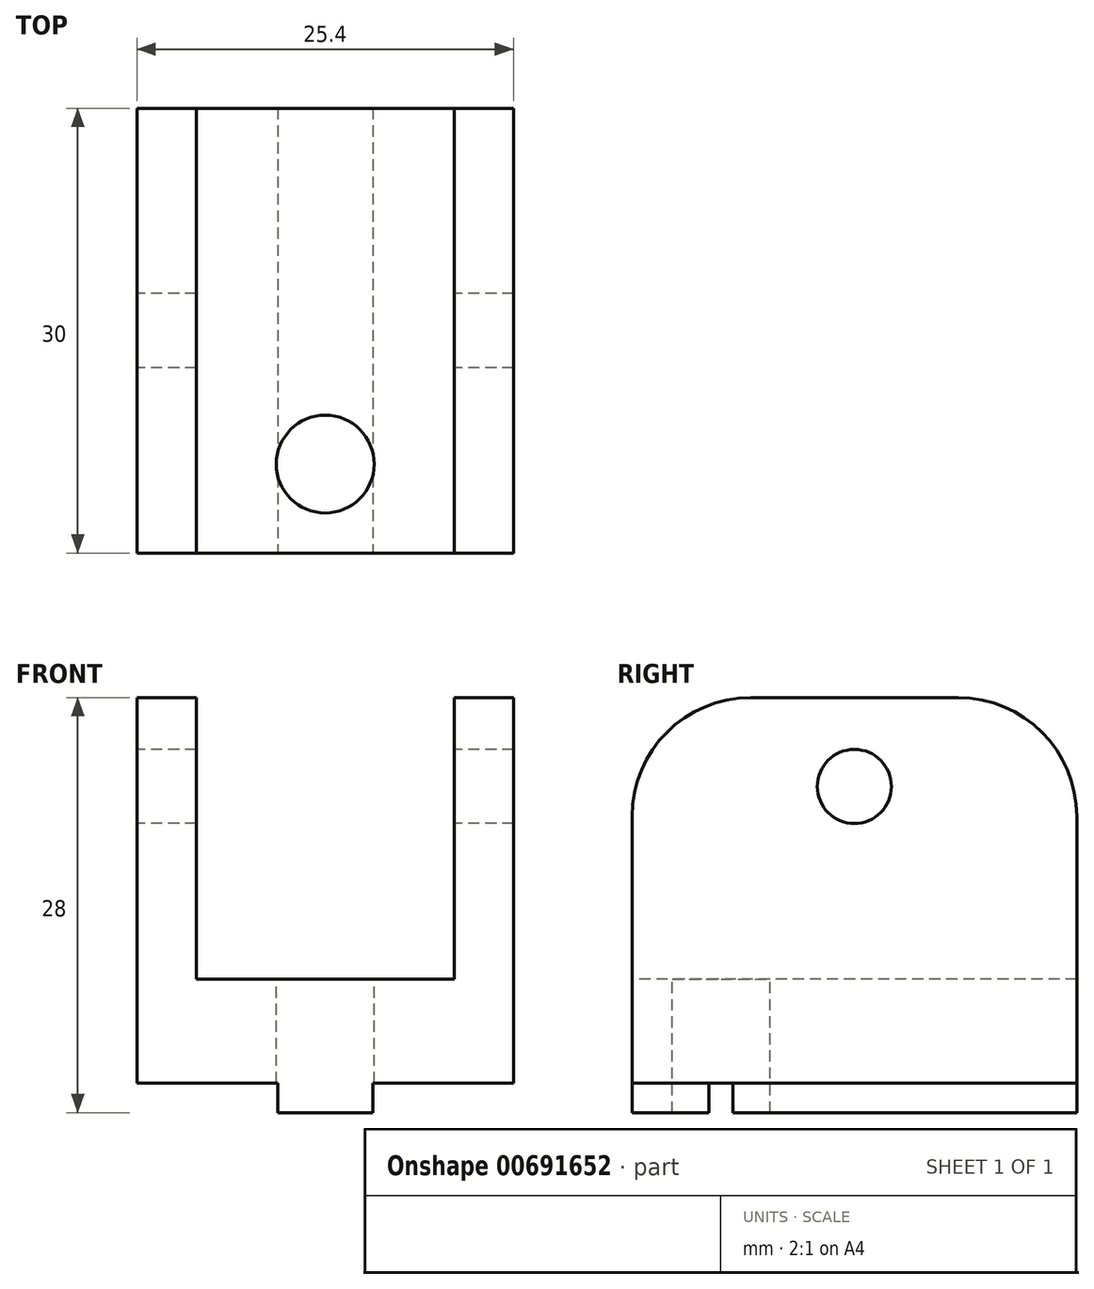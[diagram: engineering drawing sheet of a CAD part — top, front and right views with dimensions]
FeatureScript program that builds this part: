
annotation { "Feature Type Name" : "Feature", "Feature Type Description" : "" }
export const myFeature = defineFeature(function(context is Context, id is Id, definition is map)
    precondition{}
    {
        {
            var Q0;
            Q0=qCreatedBy(makeId("Right.planeOp"),FACE);
            var sketch = newSketch(context, id + "F0", { "sketchPlane" : qUnion([Q0])});
            skLineSegment(sketch, "E0.bottom", {"start": v(-7, 26) * mm, "end": v(7, 26) * mm});
            skLineSegment(sketch, "E0.top", {"start": v(-15, 0) * mm, "end": v(15, 0) * mm});
            skLineSegment(sketch, "E0.left", {"start": v(-15, 18) * mm, "end": v(-15, 0) * mm});
            skLineSegment(sketch, "E0.right", {"start": v(15, 18) * mm, "end": v(15, 0) * mm});
            skCircle(sketch, "E1", {"center": v(0, 20) * mm, "radius": 2.5 * mm});
            skPoint(sketch, "E2.visualSharp", {"position": v(-15, 26) * mm});
            skArc(sketch, "E2.filletArc", {"start": v(-7, 26) * mm, "mid": v(-12.66, 23.66) * mm, "end": v(-15, 18) * mm});
            skPoint(sketch, "E3.visualSharp", {"position": v(15, 26) * mm});
            skArc(sketch, "E3.filletArc", {"start": v(15, 18) * mm, "mid": v(12.66, 23.66) * mm, "end": v(7, 26) * mm});
            skSolve(sketch);
        }
        {
            var Q0;
            Q0=qSketchRegion(id+"F0",true);
            extrude(context, id + "F1", {"entities" : qUnion([Q0]), "depth" : 25.4 * mm, "offsetDistance" : 25 * mm});
        }
        {
            var Q0;
            Q0=makeQuery(id+"F1.opExtrude","SWEPT_FACE",FACE,{"disambiguationData":[OSD([sQuery(id+"F0.wireOp",EDGE,"E0.bottom")])]});
            var sketch = newSketch(context, id + "F2", { "sketchPlane" : qUnion([Q0])});
            skLineSegment(sketch, "E4.bottom", {"start": v(4, 18.9) * mm, "end": v(21.4, 18.9) * mm});
            skLineSegment(sketch, "E4.top", {"start": v(4, -19.7) * mm, "end": v(21.4, -19.7) * mm});
            skLineSegment(sketch, "E4.left", {"start": v(4, 18.9) * mm, "end": v(4, -19.7) * mm});
            skLineSegment(sketch, "E4.right", {"start": v(21.4, 18.9) * mm, "end": v(21.4, -19.7) * mm});
            skSolve(sketch);
        }
        {
            var Q0;
            Q0=qSketchRegion(id+"F2",true);
            extrude(context, id + "F3", {"entities" : qUnion([Q0]), "operationType" : NewBodyOperationType.REMOVE, "oppositeDirection" : true, "depth" : 19 * mm, "offsetDistance" : 25 * mm});
        }
        {
            var Q0;
            Q0=makeQuery(id+"F1.opExtrude","SWEPT_FACE",FACE,{"disambiguationData":[OSD([sQuery(id+"F0.wireOp",EDGE,"E0.top")])]});
            var sketch = newSketch(context, id + "F4", { "sketchPlane" : qUnion([Q0])});
            skLineSegment(sketch, "E5.bottom", {"start": v(15.9, -15) * mm, "end": v(9.5, -15) * mm});
            skLineSegment(sketch, "E5.top", {"start": v(15.9, 15) * mm, "end": v(9.5, 15) * mm});
            skLineSegment(sketch, "E5.left", {"start": v(15.9, -15) * mm, "end": v(15.9, 15) * mm});
            skLineSegment(sketch, "E5.right", {"start": v(9.5, -15) * mm, "end": v(9.5, 15) * mm});
            skLineSegment(sketch, "E6", {"start": v(12.7, -15) * mm, "end": v(12.7, 15) * mm, "construction": true});
            skLineSegment(sketch, "E7", {"start": v(12.7, 15) * mm, "end": v(13.72, 14.46) * mm, "construction": true});
            skSolve(sketch);
        }
        {
            var Q0;
            Q0=qSketchRegion(id+"F4",true);
            extrude(context, id + "F5", {"entities" : qUnion([Q0]), "operationType" : NewBodyOperationType.ADD, "depth" : 2 * mm, "offsetDistance" : 25 * mm});
        }
        {
            var Q0;
            Q0=makeQuery(id+"F3.boolean.opBoolean","COPY",FACE,{"derivedFrom":makeQuery(id+"F3.opExtrude","CAP_FACE",FACE,{"disambiguationData":[OSD([sQuery(id+"F2.wireOp",EDGE,"E4.bottom"),sQuery(id+"F2.wireOp",EDGE,"E4.top"),sQuery(id+"F2.wireOp",EDGE,"E4.left"),sQuery(id+"F2.wireOp",EDGE,"E4.right")])],"isStart":false})});
            var sketch = newSketch(context, id + "F6", { "sketchPlane" : qUnion([Q0])});
            skCircle(sketch, "E8", {"center": v(12.7, -9) * mm, "radius": 3.3 * mm});
            skSolve(sketch);
        }
        {
            var Q0;
            Q0=qSketchRegion(id+"F6",true);
            extrude(context, id + "F7", {"entities" : qUnion([Q0]), "operationType" : NewBodyOperationType.REMOVE, "oppositeDirection" : true, "depth" : 10 * mm, "offsetDistance" : 25 * mm});
        }
    });
